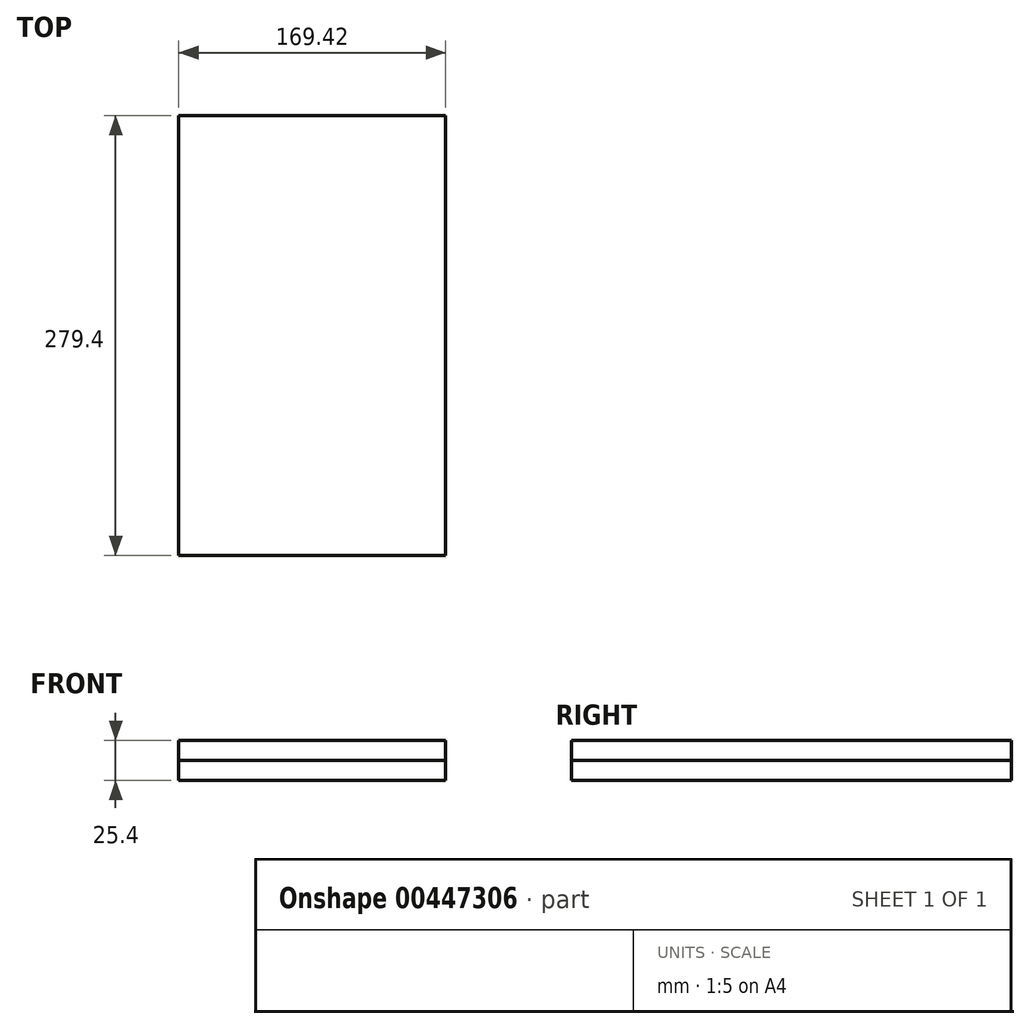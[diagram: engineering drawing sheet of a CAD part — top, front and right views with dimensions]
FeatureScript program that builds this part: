
annotation { "Feature Type Name" : "Feature", "Feature Type Description" : "" }
export const myFeature = defineFeature(function(context is Context, id is Id, definition is map)
    precondition{}
    {
        {
            var Q0;
            Q0=qCreatedBy(makeId("Top.planeOp"),FACE);
            var sketch = newSketch(context, id + "F0", { "sketchPlane" : qUnion([Q0])});
            skLineSegment(sketch, "E0.bottom", {"start": v(-84.7, 139.7) * mm, "end": v(84.7, 139.7) * mm});
            skLineSegment(sketch, "E0.top", {"start": v(-84.7, -139.7) * mm, "end": v(84.7, -139.7) * mm});
            skLineSegment(sketch, "E0.left", {"start": v(-84.7, 139.7) * mm, "end": v(-84.7, -139.7) * mm});
            skLineSegment(sketch, "E0.right", {"start": v(84.7, 139.7) * mm, "end": v(84.7, -139.7) * mm});
            skPoint(sketch, "E0.middle", {"position": v(0, 0) * mm});
            skSolve(sketch);
        }
        {
            var Q0;
            Q0 = qSketchRegion(id + "F0", true);
            extrude(context, id + "F1", {"entities" : qUnion([Q0]), "depth" : 12.7 * mm});
        }
        {
            var Q0;
            Q0 = qSketchRegion(id + "F0", true);
            extrude(context, id + "F2", {"entities" : qUnion([Q0]), "operationType" : NewBodyOperationType.ADD, "depth" : 12.7 * mm});
        }
        {
            var Q0;
            Q0=makeQuery(id+"F0.imprint","IMPRINT",FACE,{"disambiguationData":[TD([[makeQuery(id+"F0.imprint","IMPRINT",EDGE,{"derivedFrom":sQuery(id+"F0.wireOp",EDGE,"E0.bottom")}),-1.0]])]});
            extrude(context, id + "F3", {"entities" : qUnion([Q0]), "depth" : 25.4 * mm});
        }
    });
